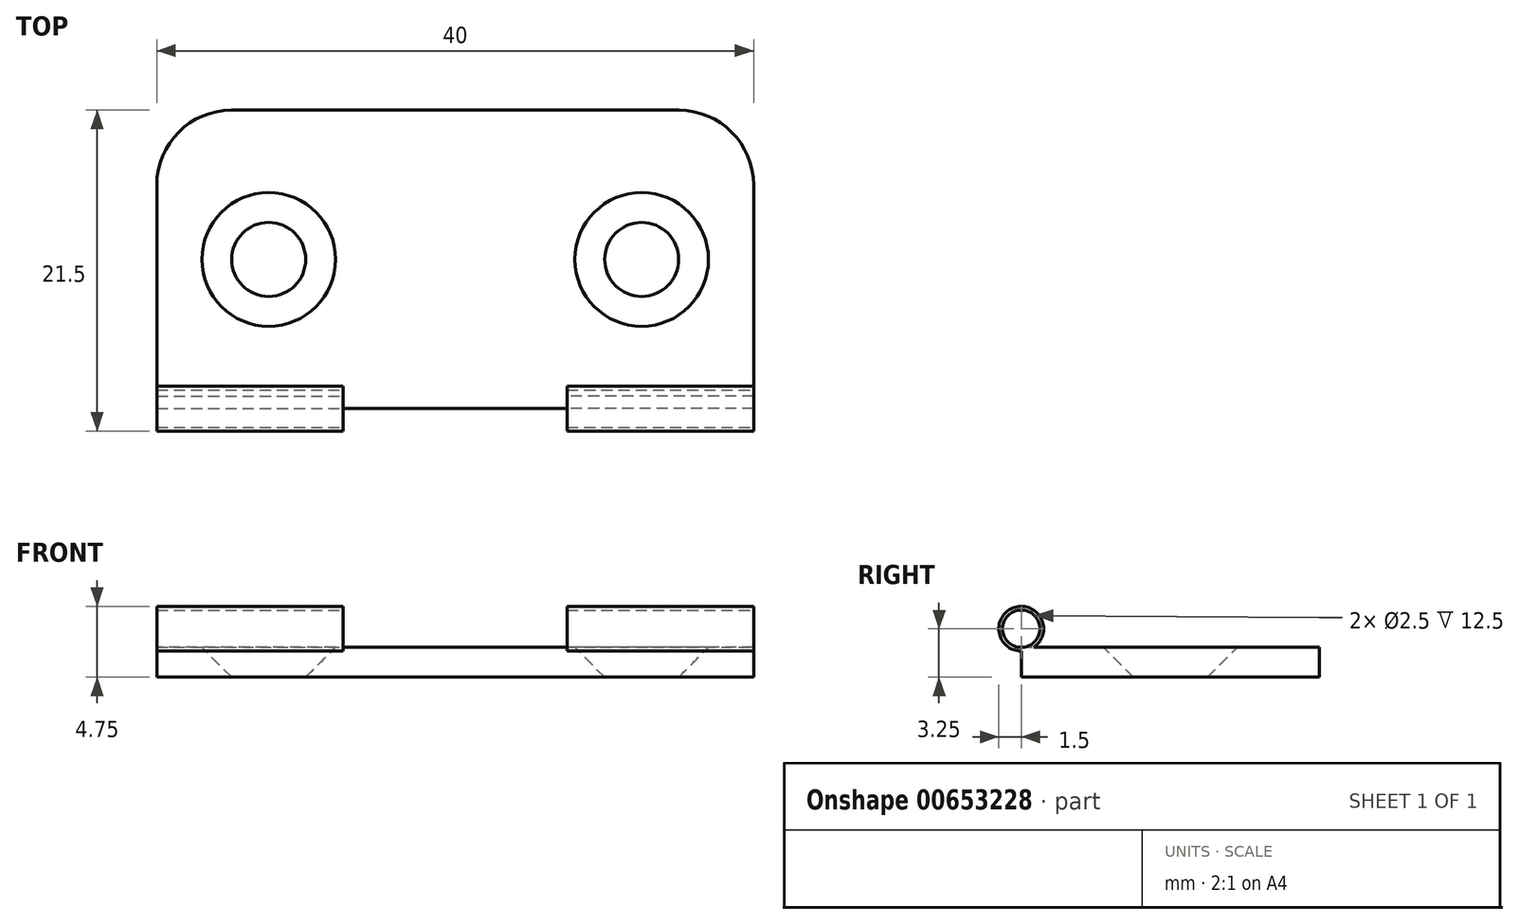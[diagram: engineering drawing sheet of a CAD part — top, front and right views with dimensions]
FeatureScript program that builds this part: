
annotation { "Feature Type Name" : "Feature", "Feature Type Description" : "" }
export const myFeature = defineFeature(function(context is Context, id is Id, definition is map)
    precondition{}
    {
        {
            var Q0;
            Q0=qCreatedBy(makeId("Top.planeOp"),FACE);
            var sketch = newSketch(context, id + "F0", { "sketchPlane" : qUnion([Q0])});
            skLineSegment(sketch, "E0.bottom", {"start": v(15, 10) * mm, "end": v(-15, 10) * mm});
            skLineSegment(sketch, "E0.top", {"start": v(20, -10) * mm, "end": v(-20, -10) * mm});
            skLineSegment(sketch, "E0.left", {"start": v(20, 5) * mm, "end": v(20, -10) * mm});
            skLineSegment(sketch, "E0.right", {"start": v(-20, 5) * mm, "end": v(-20, -10) * mm});
            skPoint(sketch, "E0.middle", {"position": v(0, 0) * mm});
            skPoint(sketch, "E1.visualSharp", {"position": v(-20, 10) * mm});
            skArc(sketch, "E1.filletArc", {"start": v(-15, 10) * mm, "mid": v(-18.54, 8.54) * mm, "end": v(-20, 5) * mm});
            skPoint(sketch, "E2.visualSharp", {"position": v(20, 10) * mm});
            skArc(sketch, "E2.filletArc", {"start": v(20, 5) * mm, "mid": v(18.54, 8.54) * mm, "end": v(15, 10) * mm});
            skSolve(sketch);
        }
        {
            var Q0;
            Q0 = qSketchRegion(id + "F0", true);
            extrude(context, id + "F1", {"entities" : qUnion([Q0]), "depth" : 2 * mm, "offsetDistance" : 25 * mm});
        }
        {
            var Q0;
            Q0=makeQuery(id+"F1.opExtrude","SWEPT_FACE",FACE,{"disambiguationData":[OSD([sQuery(id+"F0.wireOp",EDGE,"E0.left")])]});
            cPlane(context, id + "F2", {"entities" : qUnion([Q0]), "cplaneType" : CPlaneType.OFFSET, "offset" : 12.5 * mm, "oppositeDirection" : true, "width" : 150 * mm, "height" : 150 * mm});
        }
        {
            var Q0;
            Q0=qCreatedBy(id+"F2.planeOp",FACE);
            var sketch = newSketch(context, id + "F3", { "sketchPlane" : qUnion([Q0])});
            skLineSegment(sketch, "E3.0", {"start": v(5, 2) * mm, "end": v(-10, 2) * mm, "construction": true});
            skLineSegment(sketch, "E4.0", {"start": v(-10, 2) * mm, "end": v(-10, 0) * mm, "construction": true});
            skCircle(sketch, "E5", {"center": v(-10, 3.25) * mm, "radius": 1.5 * mm});
            skSolve(sketch);
        }
        {
            var Q0;
            Q0=qCreatedBy(id+"F2.planeOp",FACE);
            cPlane(context, id + "F4", {"entities" : qUnion([Q0]), "cplaneType" : CPlaneType.OFFSET, "offset" : 15 * mm, "oppositeDirection" : true, "width" : 150 * mm, "height" : 150 * mm});
        }
        {
            var Q0;
            Q0=qCreatedBy(id+"F4.planeOp",FACE);
            var sketch = newSketch(context, id + "F5", { "sketchPlane" : qUnion([Q0])});
            skPoint(sketch, "E6.0", {"position": v(-10, 1) * mm});
            skLineSegment(sketch, "E7.0", {"start": v(-10, 2) * mm, "end": v(-10, 0) * mm, "construction": true});
            skLineSegment(sketch, "E8.0", {"start": v(5, 2) * mm, "end": v(-10, 2) * mm, "construction": true});
            skCircle(sketch, "E9", {"center": v(-10, 3.25) * mm, "radius": 1.5 * mm});
            skSolve(sketch);
        }
        {
            var Q0;
            Q0 = qSketchRegion(id + "F3", true);
            var Q1;
            Q1=makeQuery(id+"F1.opExtrude","SWEPT_FACE",FACE,{"disambiguationData":[OSD([sQuery(id+"F0.wireOp",EDGE,"E0.left")])]});
            extrude(context, id + "F6", {"entities" : qUnion([Q0]), "operationType" : NewBodyOperationType.ADD, "endBound" : BoundingType.UP_TO_SURFACE, "depth" : 25 * mm, "endBoundEntityFace" : qUnion([Q1]), "offsetDistance" : 25 * mm});
        }
        {
            var Q0;
            Q0=makeQuery(id+"F5.imprint","IMPRINT",FACE,{"disambiguationData":[TD([[makeQuery(id+"F5.imprint","IMPRINT",EDGE,{"derivedFrom":sQuery(id+"F5.wireOp",EDGE,"E9")}),1.0]])]});
            var Q1;
            Q1 = qConstructionFilter(qBodyType(qCreatedBy(id + "F5" ,EDGE), BodyType.WIRE), ConstructionObject.NO);
            var Q2;
            Q2=makeQuery(id+"F1.opExtrude","SWEPT_FACE",FACE,{"disambiguationData":[OSD([sQuery(id+"F0.wireOp",EDGE,"E0.right")])]});
            extrude(context, id + "F7", {"entities" : qUnion([Q0]), "operationType" : NewBodyOperationType.ADD, "surfaceEntities" : qUnion([Q1]), "endBound" : BoundingType.UP_TO_SURFACE, "oppositeDirection" : true, "depth" : 25 * mm, "endBoundEntityFace" : qUnion([Q2]), "offsetDistance" : 25 * mm});
        }
        {
            var Q0;
            {var subQ0=sQuery(id+"F0.wireOp",EDGE,"E0.left");Q0=makeQuery(id+"F6.boolean.opBoolean","MERGE",FACE,{"derivedFrom":[makeQuery(id+"F1.opExtrude","SWEPT_FACE",FACE,{"disambiguationData":[OSD([subQ0])]}),makeQuery(id+"F6.opExtrude","CAP_FACE",FACE,{"disambiguationData":[OSD([subQ0])],"isStart":false})]});}
            var sketch = newSketch(context, id + "F8", { "sketchPlane" : qUnion([Q0])});
            skArc(sketch, "E10.0", {"start": v(-9.17, 2) * mm, "mid": v(-10.43, 4.69) * mm, "end": v(-10, 1.75) * mm, "construction": true});
            skCircle(sketch, "E11", {"center": v(-10, 3.25) * mm, "radius": 1.25 * mm});
            skSolve(sketch);
        }
        {
            var Q0;
            Q0 = qSketchRegion(id + "F8", true);
            var Q1;
            {var subQ0=sQuery(id+"F0.wireOp",EDGE,"E0.right");Q1=makeQuery(id+"F7.boolean.opBoolean","MERGE",FACE,{"derivedFrom":[makeQuery(id+"F1.opExtrude","SWEPT_FACE",FACE,{"disambiguationData":[OSD([subQ0])]}),makeQuery(id+"F7.opExtrude","CAP_FACE",FACE,{"disambiguationData":[OSD([subQ0])],"isStart":false})]});}
            extrude(context, id + "F9", {"entities" : qUnion([Q0]), "operationType" : NewBodyOperationType.REMOVE, "endBound" : BoundingType.UP_TO_SURFACE, "oppositeDirection" : true, "depth" : 25 * mm, "endBoundEntityFace" : qUnion([Q1]), "offsetDistance" : 25 * mm});
        }
        {
            var Q0;
            Q0=makeQuery(id+"F1.opExtrude","CAP_FACE",FACE,{"disambiguationData":[OSD([sQuery(id+"F0.wireOp",EDGE,"E0.bottom"),sQuery(id+"F0.wireOp",EDGE,"E0.top"),sQuery(id+"F0.wireOp",EDGE,"E0.left"),sQuery(id+"F0.wireOp",EDGE,"E0.right"),sQuery(id+"F0.wireOp",EDGE,"E1.filletArc"),sQuery(id+"F0.wireOp",EDGE,"E2.filletArc")])],"isStart":false});
            var sketch = newSketch(context, id + "F10", { "sketchPlane" : qUnion([Q0])});
            skPoint(sketch, "E12", {"position": v(-12.5, 0) * mm});
            skPoint(sketch, "E13", {"position": v(12.5, 0) * mm});
            skSolve(sketch);
        }
        {
            var Q0;
            Q0=sQuery(id+"F10.wireOp",VERTEX,"E12");
            var Q1;
            Q1=sQuery(id+"F10.wireOp",VERTEX,"E13");
            var Q2;
            Q2=makeQuery(id+"F1.opExtrude","SWEPT_BODY",BODY,{"disambiguationData":[OSD([sQuery(id+"F0.wireOp",EDGE,"E0.bottom"),sQuery(id+"F0.wireOp",EDGE,"E0.top"),sQuery(id+"F0.wireOp",EDGE,"E0.left"),sQuery(id+"F0.wireOp",EDGE,"E0.right"),sQuery(id+"F0.wireOp",EDGE,"E1.filletArc"),sQuery(id+"F0.wireOp",EDGE,"E2.filletArc")])]});
            hole(context, id + "F11", {"style" : HoleStyle.C_SINK, "endStyle" : HoleEndStyle.BLIND, "standardTappedOrClearance" : lookupTablePath({ "standard" : "ISO", "fit" : "Normal", "size" : "M4", "type" : "Clearance" }), "standardBlindInLast" : lookupTablePath({ "fit" : "Standard", "standard" : "ISO", "size" : "M4", "type" : "Clearance" }), "holeDiameter" : 4.4 * mm, "cSinkDiameter" : 8.96 * mm, "cSinkAngle" : 90 * degree, "majorDiameter" : 4 * mm, "holeDepth" : 14.1 * mm, "isTappedThrough" : true, "tappedDepth" : 12 * mm, "tapClearance" : 3, "startFromSketch" : true, "locations" : qUnion([Q0, Q1]), "scope" : qUnion([Q2])});
        }
    });
